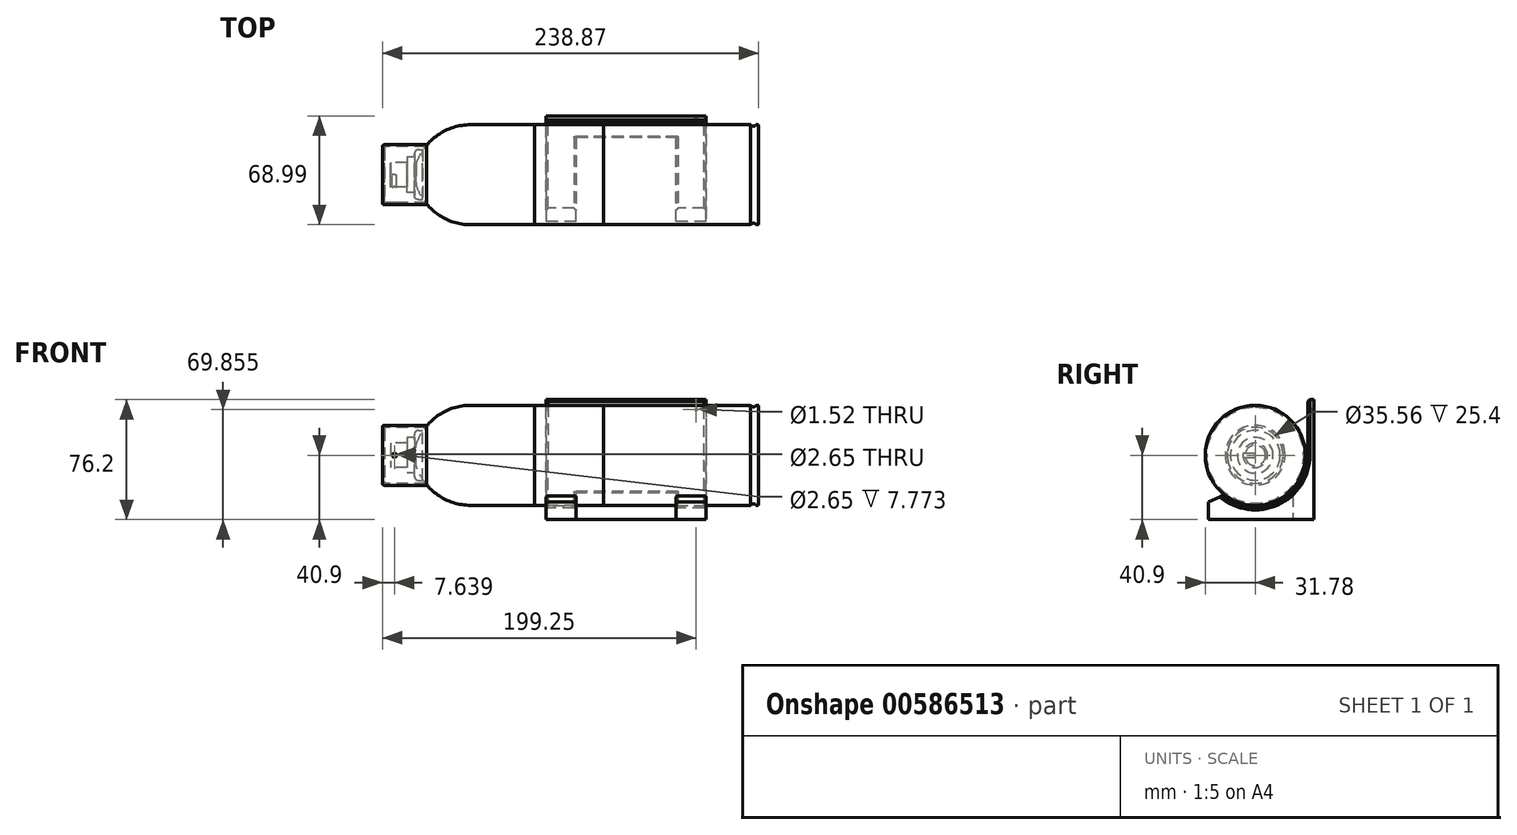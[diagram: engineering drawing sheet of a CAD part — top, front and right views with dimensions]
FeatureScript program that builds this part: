
annotation { "Feature Type Name" : "Feature", "Feature Type Description" : "" }
export const myFeature = defineFeature(function(context is Context, id is Id, definition is map)
    precondition{}
    {
        {
            var Q0;
            Q0=qCreatedBy(makeId("Right.planeOp"),FACE);
            var sketch = newSketch(context, id + "F0", { "sketchPlane" : qUnion([Q0])});
            skCircle(sketch, "E0", {"center": v(0, 0) * mm, "radius": 33.4 * mm, "construction": true});
            skLineSegment(sketch, "E1", {"start": v(33.4, 0) * mm, "end": v(33.4, 35.3) * mm});
            skLineSegment(sketch, "E2", {"start": v(33.4, 35.3) * mm, "end": v(37.21, 35.3) * mm});
            skLineSegment(sketch, "E3", {"start": v(37.21, 35.3) * mm, "end": v(37.21, -40.9) * mm});
            skLineSegment(sketch, "E4", {"start": v(37.21, -40.9) * mm, "end": v(-29.59, -40.9) * mm});
            skLineSegment(sketch, "E5", {"start": v(-29.59, -40.9) * mm, "end": v(-29.59, -15.5) * mm});
            skArc(sketch, "E6", {"start": v(33.4, 0) * mm, "mid": v(7.98, -32.43) * mm, "end": v(-29.59, -15.5) * mm});
            skSolve(sketch);
        }
        {
            var Q0;
            Q0=makeQuery(id+"F0.imprint","IMPRINT",FACE,{"disambiguationData":[TD([[makeQuery(id+"F0.imprint","IMPRINT",EDGE,{"derivedFrom":sQuery(id+"F0.wireOp",EDGE,"E1")}),-1.0]])]});
            extrude(context, id + "F1", {"entities" : qUnion([Q0]), "endBound" : BoundingType.SYMMETRIC, "depth" : 101.6 * mm, "offsetDistance" : 25.4 * mm});
        }
        {
            var Q0;
            Q0=makeQuery(id+"F1.opExtrude","SWEPT_EDGE",EDGE,{"disambiguationData":[OSD([sQuery(id+"F0.wireOp",EDGE,"E5"),sQuery(id+"F0.wireOp",EDGE,"E6")])]});
            chamfer(context, id + "F2", {"entities" : qUnion([Q0]), "width" : 5.08 * mm, "tangentPropagation" : true});
        }
        {
            var Q0;
            Q0=makeQuery(id+"F1.opExtrude","SWEPT_FACE",FACE,{"disambiguationData":[OSD([sQuery(id+"F0.wireOp",EDGE,"E4")])]});
            var sketch = newSketch(context, id + "F3", { "sketchPlane" : qUnion([Q0])});
            skLineSegment(sketch, "E7.bottom", {"start": v(-31.75, 29.59) * mm, "end": v(31.75, 29.59) * mm});
            skLineSegment(sketch, "E7.top", {"start": v(-31.75, -23.79) * mm, "end": v(31.75, -23.79) * mm});
            skLineSegment(sketch, "E7.left", {"start": v(-31.75, 29.59) * mm, "end": v(-31.75, -23.79) * mm});
            skLineSegment(sketch, "E7.right", {"start": v(31.75, 29.59) * mm, "end": v(31.75, -23.79) * mm});
            skSolve(sketch);
        }
        {
            var Q0;
            Q0 = qSketchRegion(id + "F3", true);
            extrude(context, id + "F4", {"entities" : qUnion([Q0]), "operationType" : NewBodyOperationType.REMOVE, "oppositeDirection" : true, "depth" : 25.4 * mm, "offsetDistance" : 25.4 * mm});
        }
        {
            var Q0;
            Q0=makeQuery(id+"F4.boolean.opBoolean","INTERSECT",EDGE,{"derivedFrom":[makeQuery(id+"F1.opExtrude","SWEPT_FACE",FACE,{"disambiguationData":[OSD([sQuery(id+"F0.wireOp",EDGE,"E6")])]}),makeQuery(id+"F4.opExtrude","SWEPT_FACE",FACE,{"disambiguationData":[OSD([sQuery(id+"F3.wireOp",EDGE,"E7.left")])]})]});
            var Q1;
            Q1=makeQuery(id+"F4.boolean.opBoolean","INTERSECT",EDGE,{"derivedFrom":[makeQuery(id+"F1.opExtrude","SWEPT_FACE",FACE,{"disambiguationData":[OSD([sQuery(id+"F0.wireOp",EDGE,"E6")])]}),makeQuery(id+"F4.opExtrude","SWEPT_FACE",FACE,{"disambiguationData":[OSD([sQuery(id+"F3.wireOp",EDGE,"E7.top")])]})]});
            var Q2;
            Q2=makeQuery(id+"F4.boolean.opBoolean","INTERSECT",EDGE,{"derivedFrom":[makeQuery(id+"F1.opExtrude","SWEPT_FACE",FACE,{"disambiguationData":[OSD([sQuery(id+"F0.wireOp",EDGE,"E6")])]}),makeQuery(id+"F4.opExtrude","SWEPT_FACE",FACE,{"disambiguationData":[OSD([sQuery(id+"F3.wireOp",EDGE,"E7.right")])]})]});
            var Q3;
            Q3=makeQuery(id+"F1.opExtrude","CAP_EDGE",EDGE,{"disambiguationData":[OSD([sQuery(id+"F0.wireOp",EDGE,"E6")])],"isStart":false});
            var Q4;
            Q4=makeQuery(id+"F1.opExtrude","CAP_EDGE",EDGE,{"disambiguationData":[OSD([sQuery(id+"F0.wireOp",EDGE,"E6")])],"isStart":true});
            var Q5;
            Q5=makeQuery(id+"F1.opExtrude","SWEPT_EDGE",EDGE,{"disambiguationData":[OSD([sQuery(id+"F0.wireOp",EDGE,"E1"),sQuery(id+"F0.wireOp",EDGE,"E2")])]});
            chamfer(context, id + "F5", {"entities" : qUnion([Q0, Q1, Q2, Q3, Q4, Q5]), "width" : 1.27 * mm, "tangentPropagation" : true});
        }
        {
            var Q0;
            Q0=makeQuery(id+"F1.opExtrude","SWEPT_FACE",FACE,{"disambiguationData":[OSD([sQuery(id+"F0.wireOp",EDGE,"E3")])]});
            var sketch = newSketch(context, id + "F6", { "sketchPlane" : qUnion([Q0])});
            skCircle(sketch, "E8", {"center": v(-44.45, 28.95) * mm, "radius": 0.76 * mm});
            skSolve(sketch);
        }
        {
            var Q0;
            Q0 = qSketchRegion(id + "F6", true);
            extrude(context, id + "F7", {"entities" : qUnion([Q0]), "operationType" : NewBodyOperationType.REMOVE, "endBound" : BoundingType.UP_TO_NEXT, "oppositeDirection" : true, "depth" : 25.4 * mm, "offsetDistance" : 25.4 * mm});
        }
        {
            var Q0;
            Q0=qCreatedBy(makeId("Front.planeOp"),FACE);
            var sketch = newSketch(context, id + "F8", { "sketchPlane" : qUnion([Q0])});
            skLineSegment(sketch, "E9", {"start": v(79, 0) * mm, "end": v(-133.43, 0) * mm});
            skLineSegment(sketch, "E10", {"start": v(-133.43, 0) * mm, "end": v(-133.43, 6.54) * mm});
            skLineSegment(sketch, "E11", {"start": v(79, 0) * mm, "end": v(79, 31.75) * mm});
            skLineSegment(sketch, "E12", {"start": v(79, 31.75) * mm, "end": v(-98.8, 31.75) * mm});
            skArc(sketch, "E13", {"start": v(-98.8, 31.75) * mm, "mid": v(-120.22, 24.78) * mm, "end": v(-133.43, 6.54) * mm});
            skSolve(sketch);
        }
        {
            var Q0;
            Q0 = qSketchRegion(id + "F8", true);
            var Q1;
            Q1=sQuery(id+"F8.wireOp",EDGE,"E9");
            revolve(context, id + "F9", {"entities" : qUnion([Q0]), "axis" : qUnion([Q1]), "revolveType" : RevolveType.FULL});
        }
        {
            var Q0;
            Q0=qCreatedBy(makeId("Front.planeOp"),FACE);
            var sketch = newSketch(context, id + "F10", { "sketchPlane" : qUnion([Q0])});
            skLineSegment(sketch, "E14", {"start": v(-129.36, 15.88) * mm, "end": v(-129.36, 0) * mm});
            skLineSegment(sketch, "E15", {"start": v(-129.36, 0) * mm, "end": v(-134.44, 0) * mm});
            skLineSegment(sketch, "E16", {"start": v(-134.44, 0) * mm, "end": v(-134.44, 15.88) * mm});
            skLineSegment(sketch, "E17", {"start": v(-134.44, 15.88) * mm, "end": v(-129.36, 15.88) * mm});
            skSolve(sketch);
        }
        {
            var Q0;
            Q0 = qSketchRegion(id + "F10", true);
            var Q1;
            Q1=sQuery(id+"F10.wireOp",EDGE,"E15");
            revolve(context, id + "F11", {"entities" : qUnion([Q0]), "axis" : qUnion([Q1]), "revolveType" : RevolveType.FULL});
        }
        {
            var Q0;
            Q0=qCreatedBy(makeId("Front.planeOp"),FACE);
            var sketch = newSketch(context, id + "F12", { "sketchPlane" : qUnion([Q0])});
            skLineSegment(sketch, "E18.bottom", {"start": v(-134.3, 0) * mm, "end": v(-138.99, 0) * mm});
            skLineSegment(sketch, "E18.top", {"start": v(-134.3, 11.35) * mm, "end": v(-138.99, 11.35) * mm});
            skLineSegment(sketch, "E18.left", {"start": v(-134.3, 0) * mm, "end": v(-134.3, 11.35) * mm});
            skLineSegment(sketch, "E19", {"start": v(-138.99, 11.35) * mm, "end": v(-138.99, 7.77) * mm});
            skLineSegment(sketch, "E20", {"start": v(-138.99, 7.77) * mm, "end": v(-149.62, 7.77) * mm});
            skLineSegment(sketch, "E21", {"start": v(-149.62, 7.77) * mm, "end": v(-149.62, 0) * mm});
            skLineSegment(sketch, "E22", {"start": v(-149.62, 0) * mm, "end": v(-138.99, 0) * mm});
            skSolve(sketch);
        }
        {
            var Q0;
            Q0 = qSketchRegion(id + "F12", true);
            var Q1;
            Q1=sQuery(id+"F12.wireOp",EDGE,"E22");
            revolve(context, id + "F13", {"entities" : qUnion([Q0]), "axis" : qUnion([Q1]), "revolveType" : RevolveType.FULL});
        }
        {
            var Q0;
            Q0=makeQuery(id+"F11.opRevolve","SWEPT_EDGE",EDGE,{"disambiguationData":[OSD([sQuery(id+"F10.wireOp",EDGE,"E16"),sQuery(id+"F10.wireOp",EDGE,"E17")])]});
            fillet(context, id + "F14", {"entities" : qUnion([Q0]), "radius" : 2.54 * mm, "tangentPropagation" : true, "allowEdgeOverflow" : false});
        }
        {
            var Q0;
            Q0=qCreatedBy(makeId("Front.planeOp"),FACE);
            var sketch = newSketch(context, id + "F15", { "sketchPlane" : qUnion([Q0])});
            skLineSegment(sketch, "E23", {"start": v(-154.8, 0) * mm, "end": v(-154.8, 17.78) * mm});
            skLineSegment(sketch, "E24", {"start": v(-153.53, 19.05) * mm, "end": v(-126.86, 19.05) * mm});
            skLineSegment(sketch, "E25.0", {"start": v(-152.26, 17.78) * mm, "end": v(-126.86, 17.78) * mm});
            skLineSegment(sketch, "E25.1", {"start": v(-153.53, 0) * mm, "end": v(-153.53, 16.5) * mm});
            skLineSegment(sketch, "E26", {"start": v(-126.86, 19.05) * mm, "end": v(-126.86, 17.78) * mm});
            skLineSegment(sketch, "E27", {"start": v(-154.8, 0) * mm, "end": v(-153.53, 0) * mm});
            skPoint(sketch, "E28.visualSharp", {"position": v(-153.53, 17.78) * mm});
            skArc(sketch, "E28.filletArc", {"start": v(-152.26, 17.78) * mm, "mid": v(-153.15, 17.4) * mm, "end": v(-153.53, 16.5) * mm});
            skPoint(sketch, "E29.visualSharp", {"position": v(-154.8, 19.05) * mm});
            skArc(sketch, "E29.filletArc", {"start": v(-153.53, 19.05) * mm, "mid": v(-154.42, 18.68) * mm, "end": v(-154.8, 17.78) * mm});
            skSolve(sketch);
        }
        {
            var Q0;
            Q0 = qSketchRegion(id + "F15", true);
            var Q1;
            Q1=sQuery(id+"F15.wireOp",EDGE,"E27");
            revolve(context, id + "F16", {"entities" : qUnion([Q0]), "axis" : qUnion([Q1]), "revolveType" : RevolveType.FULL});
        }
        {
            var Q0;
            Q0=qCreatedBy(makeId("Front.planeOp"),FACE);
            var sketch = newSketch(context, id + "F17", { "sketchPlane" : qUnion([Q0])});
            skLineSegment(sketch, "E30.top", {"start": v(79, 0) * mm, "end": v(84.07, 0) * mm});
            skLineSegment(sketch, "E30.left", {"start": v(79, 31.75) * mm, "end": v(79, 0) * mm});
            skLineSegment(sketch, "E30.right", {"start": v(84.07, 31.75) * mm, "end": v(84.07, 0) * mm});
            skLineSegment(sketch, "E31", {"start": v(84.07, 31.75) * mm, "end": v(82.6, 31.75) * mm});
            skArc(sketch, "E32", {"start": v(79, 31.75) * mm, "mid": v(80.8, 30.79) * mm, "end": v(82.6, 31.75) * mm});
            skSolve(sketch);
        }
        {
            var Q0;
            Q0=makeQuery(id+"F17.imprint","IMPRINT",FACE,{"disambiguationData":[TD([[makeQuery(id+"F17.imprint","IMPRINT",EDGE,{"derivedFrom":sQuery(id+"F17.wireOp",EDGE,"E30.top")}),1.0]])]});
            var Q1;
            Q1=sQuery(id+"F17.wireOp",EDGE,"E30.top");
            revolve(context, id + "F18", {"entities" : qUnion([Q0]), "axis" : qUnion([Q1]), "revolveType" : RevolveType.FULL});
        }
        {
            var Q0;
            Q0=makeQuery(id+"F18.opRevolve","SWEPT_EDGE",EDGE,{"disambiguationData":[OSD([sQuery(id+"F17.wireOp",EDGE,"E31"),sQuery(id+"F17.wireOp",EDGE,"E32")])]});
            var Q1;
            Q1=makeQuery(id+"F18.opRevolve","SWEPT_EDGE",EDGE,{"disambiguationData":[OSD([sQuery(id+"F17.wireOp",EDGE,"E30.right"),sQuery(id+"F17.wireOp",EDGE,"E31")])]});
            fillet(context, id + "F19", {"entities" : qUnion([Q0, Q1]), "radius" : 0.5 * mm, "tangentPropagation" : true, "allowEdgeOverflow" : false});
        }
        {
            var Q0;
            Q0=qCreatedBy(makeId("Front.planeOp"),FACE);
            var sketch = newSketch(context, id + "F20", { "sketchPlane" : qUnion([Q0])});
            skCircle(sketch, "E33", {"center": v(-147.16, 0) * mm, "radius": 1.33 * mm});
            skSolve(sketch);
        }
        {
            var Q0;
            Q0 = qSketchRegion(id + "F20", true);
            extrude(context, id + "F21", {"entities" : qUnion([Q0]), "operationType" : NewBodyOperationType.REMOVE, "depth" : 25.4 * mm, "offsetDistance" : 25.4 * mm});
        }
        {
            var Q0;
            Q0=qCreatedBy(makeId("Front.planeOp"),FACE);
            var sketch = newSketch(context, id + "F22", { "sketchPlane" : qUnion([Q0])});
            skLineSegment(sketch, "E34.bottom", {"start": v(-58.07, 31.78) * mm, "end": v(-14.23, 31.78) * mm});
            skLineSegment(sketch, "E34.top", {"start": v(-58.07, 0) * mm, "end": v(-14.23, 0) * mm});
            skLineSegment(sketch, "E34.left", {"start": v(-58.07, 31.78) * mm, "end": v(-58.07, 0) * mm});
            skLineSegment(sketch, "E34.right", {"start": v(-14.23, 31.78) * mm, "end": v(-14.23, 0) * mm});
            skSolve(sketch);
        }
        {
            var Q0;
            Q0 = qSketchRegion(id + "F22", true);
            var Q1;
            Q1=sQuery(id+"F22.wireOp",EDGE,"E34.top");
            revolve(context, id + "F23", {"entities" : qUnion([Q0]), "axis" : qUnion([Q1]), "revolveType" : RevolveType.FULL});
        }
    });
